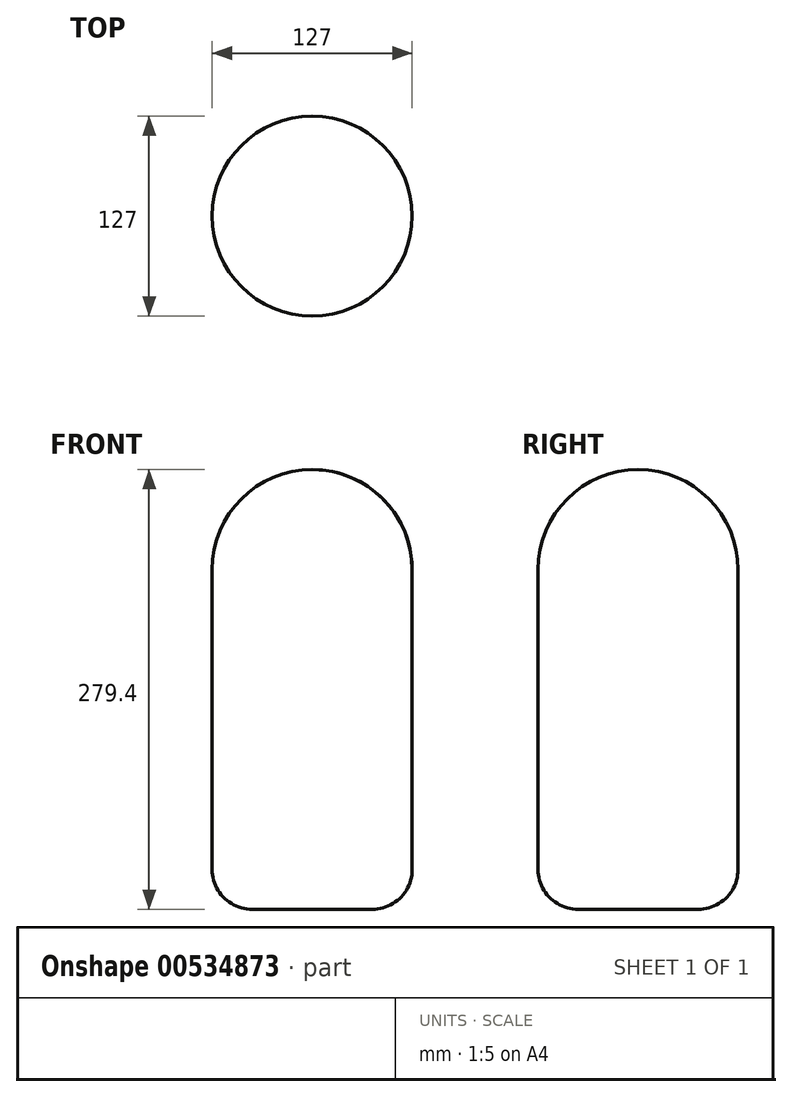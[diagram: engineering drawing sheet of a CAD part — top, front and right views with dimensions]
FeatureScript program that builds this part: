
annotation { "Feature Type Name" : "Feature", "Feature Type Description" : "" }
export const myFeature = defineFeature(function(context is Context, id is Id, definition is map)
    precondition{}
    {
        {
            var Q0;
            Q0=qCreatedBy(makeId("Top.planeOp"),FACE);
            var sketch = newSketch(context, id + "F0", { "sketchPlane" : qUnion([Q0])});
            skCircle(sketch, "E0", {"center": v(0, 0) * mm, "radius": 63.5 * mm});
            skSolve(sketch);
        }
        {
            var Q0;
            Q0=qCreatedBy(makeId("Top.planeOp"),FACE);
            cPlane(context, id + "F1", {"entities" : qUnion([Q0]), "cplaneType" : CPlaneType.OFFSET, "offset" : 101.6 * mm, "width" : 152.4 * mm, "height" : 152.4 * mm});
        }
        {
            var Q0;
            Q0=qCreatedBy(id+"F1.planeOp",FACE);
            var sketch = newSketch(context, id + "F2", { "sketchPlane" : qUnion([Q0])});
            skCircle(sketch, "E1", {"center": v(0, 0) * mm, "radius": 63.5 * mm});
            skSolve(sketch);
        }
        {
            var Q0;
            Q0=qCreatedBy(id+"F1.planeOp",FACE);
            cPlane(context, id + "F3", {"entities" : qUnion([Q0]), "cplaneType" : CPlaneType.OFFSET, "offset" : 101.6 * mm, "width" : 152.4 * mm, "height" : 152.4 * mm});
        }
        {
            var Q0;
            Q0=qCreatedBy(id+"F3.planeOp",FACE);
            var sketch = newSketch(context, id + "F4", { "sketchPlane" : qUnion([Q0])});
            skCircle(sketch, "E2", {"center": v(0, 0) * mm, "radius": 63.5 * mm});
            skSolve(sketch);
        }
        {
            var Q0;
            Q0=makeQuery(id+"F4.imprint","IMPRINT",FACE,{"disambiguationData":[TD([[makeQuery(id+"F4.imprint","IMPRINT",EDGE,{"derivedFrom":sQuery(id+"F4.wireOp",EDGE,"E2")}),1.0]])]});
            var Q1;
            Q1=makeQuery(id+"F2.imprint","IMPRINT",FACE,{"disambiguationData":[TD([[makeQuery(id+"F2.imprint","IMPRINT",EDGE,{"derivedFrom":sQuery(id+"F2.wireOp",EDGE,"E1")}),1.0]])]});
            var Q2;
            Q2=makeQuery(id+"F0.imprint","IMPRINT",FACE,{"disambiguationData":[TD([[makeQuery(id+"F0.imprint","IMPRINT",EDGE,{"derivedFrom":sQuery(id+"F0.wireOp",EDGE,"E0")}),1.0]])]});
            loft(context, id + "F5", {"sheetProfilesArray" : [{ "sheetProfileEntities" : qUnion([Q0]) }, { "sheetProfileEntities" : qUnion([Q1]) }, { "sheetProfileEntities" : qUnion([Q2]) }]});
        }
        {
            var Q0;
            Q0=makeQuery(id+"F5.opLoft","MID_CAP_EDGE",EDGE,{"disambiguationData":[OSD([sQuery(id+"F0.wireOp",EDGE,"E0"),sQuery(id+"F4.wireOp",EDGE,"E2")])],"capPos":2.0});
            fillet(context, id + "F6", {"entities" : qUnion([Q0]), "radius" : 25.4 * mm, "tangentPropagation" : true, "allowEdgeOverflow" : false});
        }
        {
            var Q0;
            Q0=qCreatedBy(id+"F3.planeOp",FACE);
            cPlane(context, id + "F7", {"entities" : qUnion([Q0]), "cplaneType" : CPlaneType.OFFSET, "offset" : 76.2 * mm, "width" : 152.4 * mm, "height" : 152.4 * mm});
        }
        {
            var Q0;
            Q0=qCreatedBy(id+"F7.planeOp",FACE);
            var sketch = newSketch(context, id + "F8", { "sketchPlane" : qUnion([Q0])});
            skCircle(sketch, "E3", {"center": v(0, 0) * mm, "radius": 63.5 * mm});
            skSolve(sketch);
        }
        {
            var Q1;
            Q1=makeQuery(id+"F4.imprint","IMPRINT",FACE,{"disambiguationData":[TD([[makeQuery(id+"F4.imprint","IMPRINT",EDGE,{"derivedFrom":sQuery(id+"F4.wireOp",EDGE,"E2")}),1.0]])]});
            var Q2;
            Q2=makeQuery(id+"F8.imprint","IMPRINT",FACE,{"disambiguationData":[TD([[makeQuery(id+"F8.imprint","IMPRINT",EDGE,{"derivedFrom":sQuery(id+"F8.wireOp",EDGE,"E3")}),1.0]])]});
            loft(context, id + "F9", {"operationType" : NewBodyOperationType.ADD, "sheetProfilesArray" : [{ "sheetProfileEntities" : qUnion([Q1]) }, { "sheetProfileEntities" : qUnion([Q2]) }]});
        }
        {
            var Q0;
            Q0=makeQuery(id+"F9.opLoft","MID_CAP_EDGE",EDGE,{"disambiguationData":[OSD([sQuery(id+"F4.wireOp",EDGE,"E2"),sQuery(id+"F8.wireOp",EDGE,"E3")])],"capPos":1.0});
            fillet(context, id + "F10", {"entities" : qUnion([Q0]), "radius" : 63.5 * mm, "tangentPropagation" : true, "allowEdgeOverflow" : false});
        }
    });
